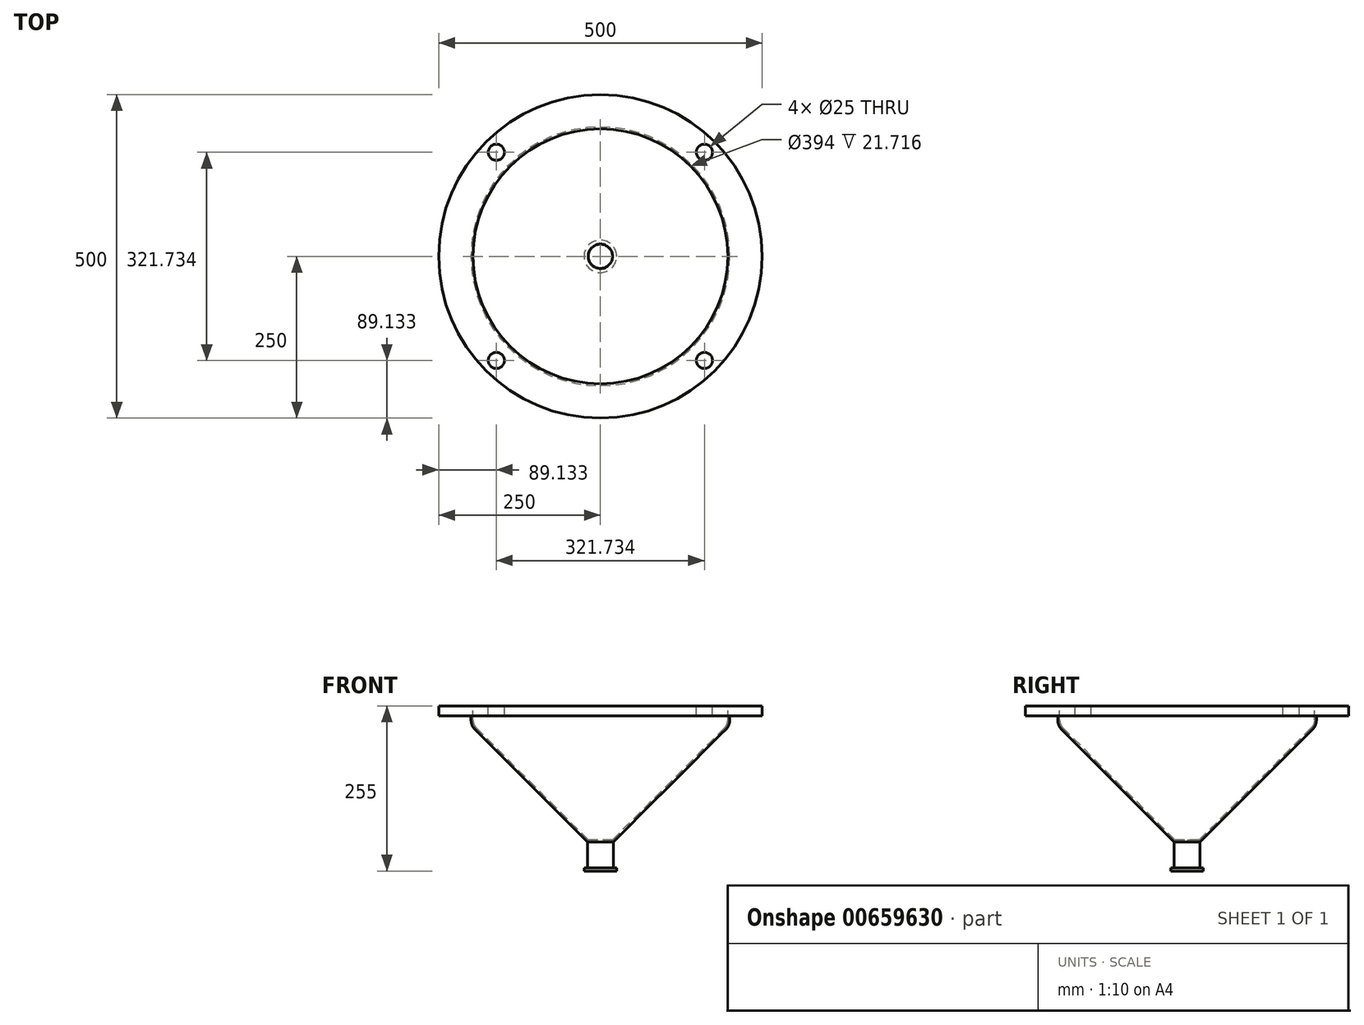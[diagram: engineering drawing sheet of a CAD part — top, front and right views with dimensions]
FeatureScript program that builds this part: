
annotation { "Feature Type Name" : "Feature", "Feature Type Description" : "" }
export const myFeature = defineFeature(function(context is Context, id is Id, definition is map)
    precondition{}
    {
        {
            var Q0;
            Q0=qCreatedBy(makeId("Top.planeOp"),FACE);
            var sketch = newSketch(context, id + "F0", { "sketchPlane" : qUnion([Q0])});
            skCircle(sketch, "E0", {"center": v(0, 0) * mm, "radius": 200 * mm});
            skCircle(sketch, "E1", {"center": v(0, 0) * mm, "radius": 250 * mm});
            skSolve(sketch);
        }
        {
            var Q0;
            Q0=qSketchRegion(id+"F0",true);
            extrude(context, id + "F1", {"entities" : qUnion([Q0]), "depth" : 15 * mm, "offsetDistance" : 25 * mm});
        }
        {
            var Q0;
            Q0=qCreatedBy(makeId("Front.planeOp"),FACE);
            var sketch = newSketch(context, id + "F2", { "sketchPlane" : qUnion([Q0])});
            skLineSegment(sketch, "E2", {"start": v(200, 15) * mm, "end": v(200, -6.72) * mm});
            skLineSegment(sketch, "E3", {"start": v(194.14, -20.86) * mm, "end": v(20, -195) * mm});
            skLineSegment(sketch, "E4", {"start": v(20, -195) * mm, "end": v(0, -195) * mm});
            skPoint(sketch, "E5.visualSharp", {"position": v(200, -15) * mm});
            skArc(sketch, "E5.filletArc", {"start": v(194.14, -20.86) * mm, "mid": v(198.48, -14.37) * mm, "end": v(200, -6.72) * mm});
            skLineSegment(sketch, "E6.0", {"start": v(18.76, -192) * mm, "end": v(0, -192) * mm});
            skLineSegment(sketch, "E6.1", {"start": v(192.02, -18.74) * mm, "end": v(18.76, -192) * mm});
            skArc(sketch, "E6.2", {"start": v(192.02, -18.74) * mm, "mid": v(195.7, -13.22) * mm, "end": v(197, -6.72) * mm});
            skLineSegment(sketch, "E6.3", {"start": v(197, 15) * mm, "end": v(197, -6.72) * mm});
            skLineSegment(sketch, "E7", {"start": v(197, 15) * mm, "end": v(200, 15) * mm});
            skLineSegment(sketch, "E8", {"start": v(0, -192) * mm, "end": v(0, -195) * mm});
            skSolve(sketch);
        }
        {
            var Q0;
            Q0=qSketchRegion(id+"F2",true);
            var Q1;
            Q1=sQuery(id+"F2.wireOp",EDGE,"E8");
            revolve(context, id + "F3", {"operationType" : NewBodyOperationType.ADD, "entities" : qUnion([Q0]), "axis" : qUnion([Q1]), "revolveType" : RevolveType.FULL});
        }
        {
            var Q0;
            Q0=makeQuery(id+"F3.boolean.opBoolean","MERGE",FACE,{"derivedFrom":[makeQuery(id+"F1.opExtrude","CAP_FACE",FACE,{"disambiguationData":[OSD([sQuery(id+"F0.wireOp",EDGE,"xTTwQilN-fKaz-kDPW-e2K0-96Pd5emqFTFM"),sQuery(id+"F0.wireOp",EDGE,"E0")])],"isStart":false}),makeQuery(id+"F3.opRevolve","SWEPT_FACE",FACE,{"disambiguationData":[OSD([sQuery(id+"F2.wireOp",EDGE,"E7")])]})]});
            var sketch = newSketch(context, id + "F4", { "sketchPlane" : qUnion([Q0])});
            skCircle(sketch, "E9", {"center": v(219.75, 58.88) * mm, "radius": 7.5 * mm});
            skLineSegment(sketch, "E10", {"start": v(219.75, 58.88) * mm, "end": v(0, 0) * mm, "construction": true});
            skLineSegment(sketch, "E11", {"start": v(0, 0) * mm, "end": v(54.06, 0) * mm, "construction": true});
            skLineSegment(sketch, "E12.1.0", {"start": v(160.87, 160.87) * mm, "end": v(0, 0) * mm, "construction": true});
            skCircle(sketch, "E12.1.1", {"center": v(160.87, 160.87) * mm, "radius": 7.5 * mm});
            skLineSegment(sketch, "E12.2.0", {"start": v(58.88, 219.75) * mm, "end": v(0, 0) * mm, "construction": true});
            skCircle(sketch, "E12.2.1", {"center": v(58.88, 219.75) * mm, "radius": 7.5 * mm});
            skLineSegment(sketch, "E12.3.0", {"start": v(-58.88, 219.75) * mm, "end": v(0, 0) * mm, "construction": true});
            skCircle(sketch, "E12.3.1", {"center": v(-58.88, 219.75) * mm, "radius": 7.5 * mm});
            skLineSegment(sketch, "E12.4.0", {"start": v(-160.87, 160.87) * mm, "end": v(0, 0) * mm, "construction": true});
            skCircle(sketch, "E12.4.1", {"center": v(-160.87, 160.87) * mm, "radius": 7.5 * mm});
            skLineSegment(sketch, "E12.5.0", {"start": v(-219.75, 58.88) * mm, "end": v(0, 0) * mm, "construction": true});
            skCircle(sketch, "E12.5.1", {"center": v(-219.75, 58.88) * mm, "radius": 7.5 * mm});
            skLineSegment(sketch, "E12.6.0", {"start": v(-219.75, -58.88) * mm, "end": v(0, 0) * mm, "construction": true});
            skCircle(sketch, "E12.6.1", {"center": v(-219.75, -58.88) * mm, "radius": 7.5 * mm});
            skLineSegment(sketch, "E12.7.0", {"start": v(-160.87, -160.87) * mm, "end": v(0, 0) * mm, "construction": true});
            skCircle(sketch, "E12.7.1", {"center": v(-160.87, -160.87) * mm, "radius": 7.5 * mm});
            skLineSegment(sketch, "E12.8.0", {"start": v(-58.88, -219.75) * mm, "end": v(0, 0) * mm, "construction": true});
            skCircle(sketch, "E12.8.1", {"center": v(-58.88, -219.75) * mm, "radius": 7.5 * mm});
            skLineSegment(sketch, "E12.9.0", {"start": v(58.88, -219.75) * mm, "end": v(0, 0) * mm, "construction": true});
            skCircle(sketch, "E12.9.1", {"center": v(58.88, -219.75) * mm, "radius": 7.5 * mm});
            skLineSegment(sketch, "E12.10.0", {"start": v(160.87, -160.87) * mm, "end": v(0, 0) * mm, "construction": true});
            skCircle(sketch, "E12.10.1", {"center": v(160.87, -160.87) * mm, "radius": 7.5 * mm});
            skLineSegment(sketch, "E12.11.0", {"start": v(219.75, -58.88) * mm, "end": v(0, 0) * mm, "construction": true});
            skCircle(sketch, "E12.11.1", {"center": v(219.75, -58.88) * mm, "radius": 7.5 * mm});
            skPoint(sketch, "E12.center", {"position": v(0, 0) * mm});
            skSolve(sketch);
        }
        {
            var Q0;
            Q0=makeQuery(id+"F3.opRevolve","SWEPT_FACE",FACE,{"disambiguationData":[OSD([sQuery(id+"F2.wireOp",EDGE,"E4")])]});
            var sketch = newSketch(context, id + "F5", { "sketchPlane" : qUnion([Q0])});
            skCircle(sketch, "E13", {"center": v(0, 0) * mm, "radius": 20 * mm});
            skSolve(sketch);
        }
        {
            var Q0;
            Q0=qSketchRegion(id+"F5",true);
            extrude(context, id + "F6", {"entities" : qUnion([Q0]), "operationType" : NewBodyOperationType.ADD, "depth" : 40 * mm, "offsetDistance" : 25 * mm});
        }
        {
            var Q0;
            Q0=makeQuery(id+"F6.opExtrude","CAP_FACE",FACE,{"disambiguationData":[OSD([sQuery(id+"F5.wireOp",EDGE,"E13")])],"isStart":false});
            var sketch = newSketch(context, id + "F7", { "sketchPlane" : qUnion([Q0])});
            skCircle(sketch, "E14", {"center": v(0, 0) * mm, "radius": 25.25 * mm});
            skSolve(sketch);
        }
        {
            var Q0;
            Q0=qSketchRegion(id+"F7",true);
            extrude(context, id + "F8", {"entities" : qUnion([Q0]), "operationType" : NewBodyOperationType.ADD, "depth" : 5 * mm, "offsetDistance" : 25 * mm});
        }
        {
            var Q0;
            Q0=makeQuery(id+"F3.boolean.opBoolean","MERGE",FACE,{"derivedFrom":[makeQuery(id+"F1.opExtrude","CAP_FACE",FACE,{"disambiguationData":[OSD([sQuery(id+"F0.wireOp",EDGE,"E0"),sQuery(id+"F0.wireOp",EDGE,"E1")])],"isStart":false}),makeQuery(id+"F3.opRevolve","SWEPT_FACE",FACE,{"disambiguationData":[OSD([sQuery(id+"F2.wireOp",EDGE,"E7")])]})]});
            var sketch = newSketch(context, id + "F9", { "sketchPlane" : qUnion([Q0])});
            skCircle(sketch, "E15", {"center": v(160.87, 160.87) * mm, "radius": 12.5 * mm});
            skCircle(sketch, "E16.1.0", {"center": v(-160.87, 160.87) * mm, "radius": 12.5 * mm});
            skCircle(sketch, "E16.2.0", {"center": v(-160.87, -160.87) * mm, "radius": 12.5 * mm});
            skCircle(sketch, "E16.3.0", {"center": v(160.87, -160.87) * mm, "radius": 12.5 * mm});
            skPoint(sketch, "E16.center", {"position": v(0, 0) * mm});
            skSolve(sketch);
        }
        {
            var Q0;
            Q0 = qSketchRegion(id + "F9", true);
            extrude(context, id + "F10", {"entities" : qUnion([Q0]), "operationType" : NewBodyOperationType.REMOVE, "oppositeDirection" : true, "depth" : 15 * mm, "offsetDistance" : 25 * mm});
        }
    });
